# Revit family: Legrand_Gestion_eclairage_Interface_KNX
name_source: partatom
category: Dispositifs d'éclairage
units: mm (PartAtom-declared; Revit-internal decimal feet)

## family parameters
Conserver l'orientation des annotations = Non
Cote de connecteur circulaire = Utiliser le diamètre
Couper avec des vides une fois chargée = Non
Hôte = Face
Partagée = Non
Point de calcul de pièce = Non
Type d'élément = Normal

## types (1)
- Radio/KNX
    Adapté pour transmission sans fil = Non
    Angle de détection horizontal (MAX) (°) = 0
    Angle de détection horizontal (MIN) (°) = 0
    Capacité de coupure max. (W) = 0
    Classe de protection (IP) = IP20
    Collecteur de terre = Non
    Condition Générale d'Utilisation = https://export.legrand.com
    Cosses d'artère secondaire = Non
    Couleur = <Par catégorie>
    Coupure forcée = Non
    Courant de démarrage max. (A) = 0
    Description = Interface faux-plafond Radio/KNX
    Diamètre de détection sur le plancher (m) = 0
    Durée d'enclenchement max. (mn) = 0
    Durée d'enclenchement min. (s) = 0
    Elévation par défaut = 1219 mm
    Entrée secondaire = Non
    Fabricant = Legrand
    Fonction variateur intégré = Non
    Fréquence (MAX) (Hz) = 0
    Fréquence (MIN) (Hz) = 0
    Gestion CVC = Non
    Gestion alarme = Non
    Hauteur de montage maximale (m) = 0
    Liaison neutre = Non
    Mode de montage = apparent
    Modèle = 048877
    Numéro RAL = 0
    Portée max. frontale (m) = 0
    Portée max. latérale (m) = 0
    Réglage de lumière constante = Non
    Sensibilité lumineuse (MAX) (lx) = 0
    Sensibilité lumineuse (MIN) (lx) = 0
    Sensibilité lumineuse réglable = Non
    Sensibilité réglable = Non
    Température (MAX) (°C) = 0
    Température (MIN) (°C) = 0
    Tension nominale (V) = 0
    Télécommandable = Non
    URL = http://www.legrandoc.com
